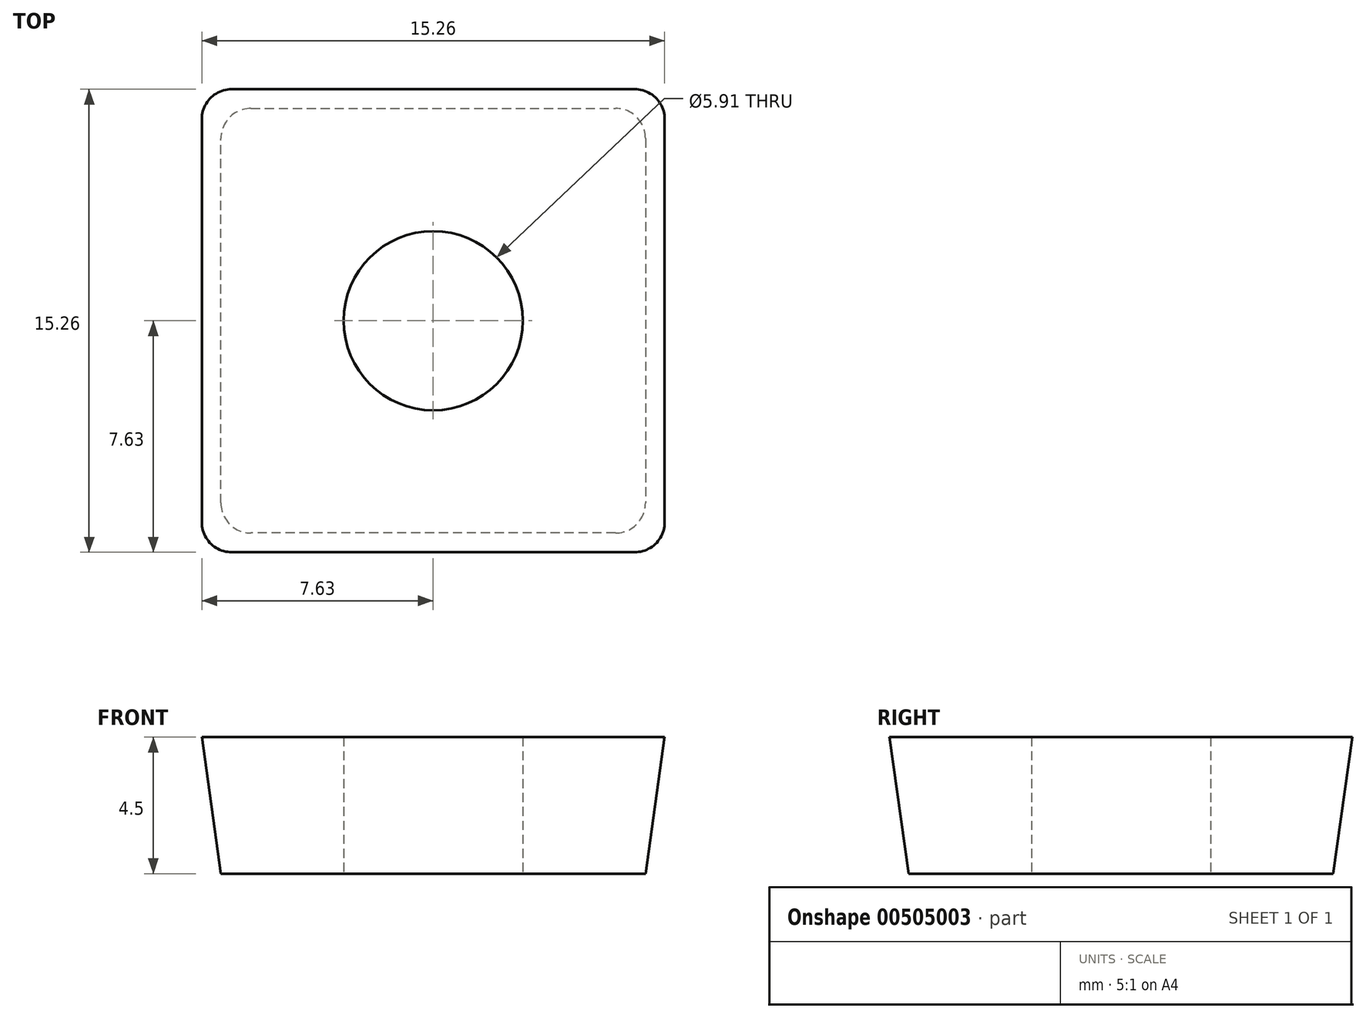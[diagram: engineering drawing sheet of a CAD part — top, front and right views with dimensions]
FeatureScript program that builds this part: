
annotation { "Feature Type Name" : "Feature", "Feature Type Description" : "" }
export const myFeature = defineFeature(function(context is Context, id is Id, definition is map)
    precondition{}
    {
        {
            var Q0;
            Q0=qCreatedBy(makeId("Top.planeOp"),FACE);
            var sketch = newSketch(context, id + "F0", { "sketchPlane" : qUnion([Q0])});
            skLineSegment(sketch, "E0.bottom", {"start": v(0, 0) * mm, "end": v(14, 0) * mm});
            skLineSegment(sketch, "E0.top", {"start": v(0, -14) * mm, "end": v(14, -14) * mm});
            skLineSegment(sketch, "E0.left", {"start": v(0, 0) * mm, "end": v(0, -14) * mm});
            skLineSegment(sketch, "E0.right", {"start": v(14, 0) * mm, "end": v(14, -14) * mm});
            skSolve(sketch);
        }
        {
            var Q0;
            Q0 = qSketchRegion(id + "F0", true);
            extrude(context, id + "F1", {"entities" : qUnion([Q0]), "depth" : 4.5 * mm, "hasDraft" : true, "draftAngle" : 8 * degree});
        }
        {
            var Q0;
            Q0=makeQuery(id+"F1.opExtrude","SWEPT_EDGE",EDGE,{"disambiguationData":[OSD([sQuery(id+"F0.wireOp",EDGE,"E0.top"),sQuery(id+"F0.wireOp",EDGE,"E0.left")])]});
            var Q1;
            Q1=makeQuery(id+"F1.opExtrude","SWEPT_EDGE",EDGE,{"disambiguationData":[OSD([sQuery(id+"F0.wireOp",EDGE,"E0.top"),sQuery(id+"F0.wireOp",EDGE,"E0.right")])]});
            var Q2;
            Q2=makeQuery(id+"F1.opExtrude","SWEPT_EDGE",EDGE,{"disambiguationData":[OSD([sQuery(id+"F0.wireOp",EDGE,"E0.bottom"),sQuery(id+"F0.wireOp",EDGE,"E0.right")])]});
            var Q3;
            Q3=makeQuery(id+"F1.opExtrude","SWEPT_EDGE",EDGE,{"disambiguationData":[OSD([sQuery(id+"F0.wireOp",EDGE,"E0.bottom"),sQuery(id+"F0.wireOp",EDGE,"E0.left")])]});
            fillet(context, id + "F2", {"entities" : qUnion([Q0, Q1, Q2, Q3]), "radius" : 1 * mm, "tangentPropagation" : true, "allowEdgeOverflow" : false});
        }
        {
            var Q0;
            Q0=makeQuery(id+"F1.opExtrude","CAP_FACE",FACE,{"disambiguationData":[OSD([sQuery(id+"F0.wireOp",EDGE,"E0.bottom"),sQuery(id+"F0.wireOp",EDGE,"E0.top"),sQuery(id+"F0.wireOp",EDGE,"E0.left"),sQuery(id+"F0.wireOp",EDGE,"E0.right")])],"isStart":true});
            var sketch = newSketch(context, id + "F3", { "sketchPlane" : qUnion([Q0])});
            skCircle(sketch, "E1", {"center": v(7, 7) * mm, "radius": 2.95 * mm});
            skSolve(sketch);
        }
        {
            var Q0;
            Q0=makeQuery(id+"F3.imprint","IMPRINT",FACE,{"disambiguationData":[TD([[makeQuery(id+"F3.imprint","IMPRINT",EDGE,{"derivedFrom":sQuery(id+"F3.wireOp",EDGE,"E1")}),1.0]])]});
            extrude(context, id + "F4", {"entities" : qUnion([Q0]), "operationType" : NewBodyOperationType.REMOVE, "oppositeDirection" : true, "depth" : 25 * mm});
        }
    });
